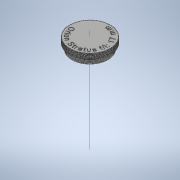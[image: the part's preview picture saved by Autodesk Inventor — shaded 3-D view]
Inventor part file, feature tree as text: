
AUTODESK INVENTOR PART (.ipt)
format: ipt  version: 2021.2 (Build 252289000, 289)  size: 8,708,608 bytes
history: native  units: in
note: dims shown in document units (in); Inventor stores cm internally (conversion verified against a paired STEP export)
features: helix x1, pattern_circular x1, plane x1, mirror x1, sketch x1
ambient origin geometry x8: Origin, YZ Plane, XZ Plane, XY Plane, X Axis, Y Axis, Z Axis, Center Point
bodies: Solid1 (feature_tree), Body1 (feature_tree)
feature tree (5):
  helix  "Coil1"  [1 undecoded]
  pattern_circular  "Circular Pattern1"  Count=72  [1 undecoded]
  plane  "Work Plane1"
  mirror  "Mirror1"
  sketch  "Sketch1"  dims[d1=0.0312in d2=1.0in d3=0.375in d4=0.0492in d5=0.0in d6=90.0deg d7=90.0deg d8=0.0in d9=0.0in d10=28.3465in d11=2.4737in d13=-0.1875in]
note: 2 required parameter values undecoded (feature->parameter linkage not recoverable at this tier; creation-order binding heuristic only, values carry confidence <= 0.55)
